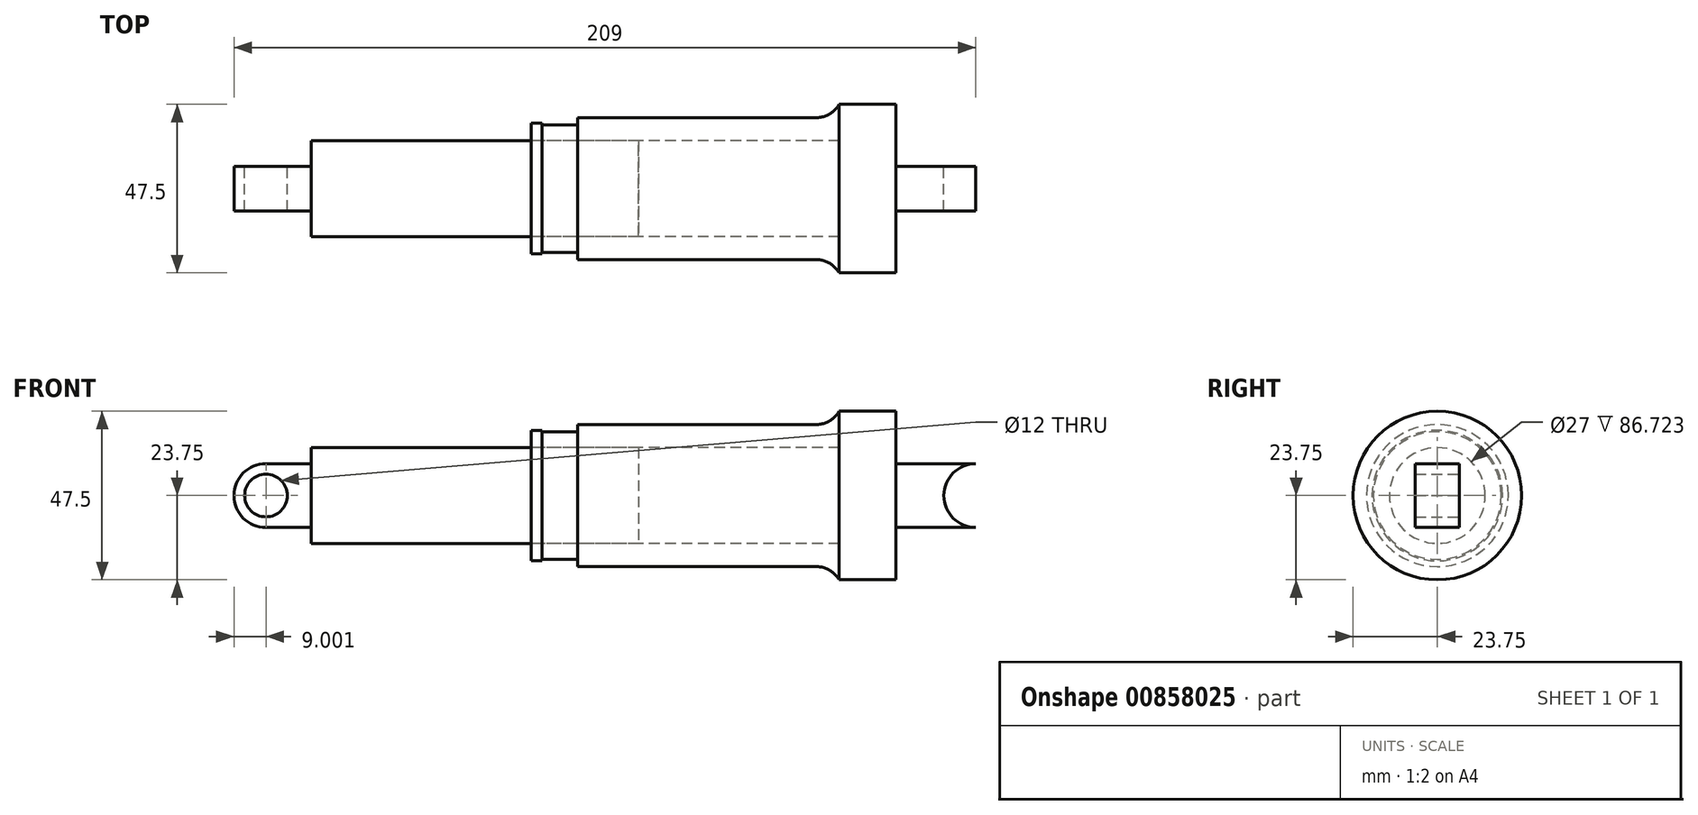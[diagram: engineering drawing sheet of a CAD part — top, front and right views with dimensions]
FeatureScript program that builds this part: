
annotation { "Feature Type Name" : "Feature", "Feature Type Description" : "" }
export const myFeature = defineFeature(function(context is Context, id is Id, definition is map)
    precondition{}
    {
        {
            var Q0;
            Q0=qCreatedBy(makeId("Front.planeOp"),FACE);
            var sketch = newSketch(context, id + "F0", { "sketchPlane" : qUnion([Q0])});
            skLineSegment(sketch, "E0.bottom", {"start": v(-74.36, -6.75) * mm, "end": v(74.36, -6.75) * mm});
            skLineSegment(sketch, "E0.top", {"start": v(-74.36, 6.75) * mm, "end": v(74.36, 6.75) * mm});
            skLineSegment(sketch, "E0.left", {"start": v(-74.36, -6.75) * mm, "end": v(-74.36, 6.75) * mm});
            skLineSegment(sketch, "E0.right", {"start": v(74.36, -6.75) * mm, "end": v(74.36, 6.75) * mm});
            skPoint(sketch, "E0.middle", {"position": v(0, 0) * mm});
            skLineSegment(sketch, "E1", {"start": v(-12.36, 6.75) * mm, "end": v(-12.36, -6.75) * mm});
            skLineSegment(sketch, "E2", {"start": v(17.86, 6.75) * mm, "end": v(17.86, -6.75) * mm});
            skLineSegment(sketch, "E3", {"start": v(-74.36, -6.75) * mm, "end": v(-87.14, -6.75) * mm});
            skLineSegment(sketch, "E4", {"start": v(-74.36, -6.75) * mm, "end": v(-74.4, -15.75) * mm});
            skLineSegment(sketch, "E5", {"start": v(-12.36, 6.75) * mm, "end": v(-12.36, 11.65) * mm});
            skLineSegment(sketch, "E6", {"start": v(-12.36, 11.65) * mm, "end": v(-9.36, 11.65) * mm});
            skLineSegment(sketch, "E7", {"start": v(-9.36, 11.65) * mm, "end": v(-9.36, 11.25) * mm});
            skLineSegment(sketch, "E8", {"start": v(-9.36, 11.25) * mm, "end": v(0.64, 11.25) * mm});
            skLineSegment(sketch, "E9", {"start": v(0.64, 11.25) * mm, "end": v(0.64, 13.25) * mm});
            skLineSegment(sketch, "E10", {"start": v(0.64, 13.25) * mm, "end": v(67.86, 13.25) * mm});
            skArc(sketch, "E11", {"start": v(67.86, 13.25) * mm, "mid": v(71.61, 14.25) * mm, "end": v(74.36, 17) * mm});
            skLineSegment(sketch, "E12", {"start": v(74.36, 17) * mm, "end": v(90.36, 17) * mm});
            skLineSegment(sketch, "E13", {"start": v(74.36, -6.75) * mm, "end": v(112.86, -6.75) * mm});
            skLineSegment(sketch, "E14", {"start": v(90.36, 17) * mm, "end": v(90.36, -6.75) * mm});
            skArc(sketch, "E15", {"start": v(112.86, 2.25) * mm, "mid": v(121.86, -6.75) * mm, "end": v(112.86, -15.75) * mm});
            skArc(sketch, "E16", {"start": v(112.86, 2.25) * mm, "mid": v(103.86, -6.75) * mm, "end": v(112.86, -15.75) * mm});
            skArc(sketch, "E17", {"start": v(-87.14, 2.25) * mm, "mid": v(-96.14, -6.75) * mm, "end": v(-87.14, -15.75) * mm});
            skPoint(sketch, "E17.startSnap0", {"position": v(-87.14, -6.75) * mm});
            skArc(sketch, "E18", {"start": v(-87.14, 2.25) * mm, "mid": v(-78.14, -6.75) * mm, "end": v(-87.14, -15.75) * mm});
            skLineSegment(sketch, "E19", {"start": v(-87.14, 2.25) * mm, "end": v(-74.36, 2.25) * mm});
            skLineSegment(sketch, "E20", {"start": v(-87.14, -15.75) * mm, "end": v(-74.4, -15.75) * mm});
            skLineSegment(sketch, "E21", {"start": v(112.86, 2.25) * mm, "end": v(90.36, 2.25) * mm});
            skLineSegment(sketch, "E22", {"start": v(112.86, -15.75) * mm, "end": v(90.36, -15.75) * mm});
            skLineSegment(sketch, "E23", {"start": v(90.36, -6.75) * mm, "end": v(90.36, -15.75) * mm});
            skArc(sketch, "E24.0", {"start": v(112.86, -0.75) * mm, "mid": v(118.86, -6.75) * mm, "end": v(112.86, -12.75) * mm});
            skArc(sketch, "E24.1", {"start": v(112.86, -0.75) * mm, "mid": v(106.86, -6.75) * mm, "end": v(112.86, -12.75) * mm});
            skArc(sketch, "E25.0", {"start": v(-87.14, -0.75) * mm, "mid": v(-93.14, -6.75) * mm, "end": v(-87.14, -12.75) * mm});
            skArc(sketch, "E25.1", {"start": v(-87.14, -0.75) * mm, "mid": v(-81.14, -6.75) * mm, "end": v(-87.14, -12.75) * mm});
            skSolve(sketch);
        }
        {
            var Q0;
            {var subQ3=sQuery(id+"F0.wireOp",EDGE,"E0.right");Q0=makeQuery(id+"F0.imprint","IMPRINT",FACE,{"disambiguationData":[TD([[makeQuery(id+"F0.imprint","IMPRINT",EDGE,{"derivedFrom":subQ3}),-1.0]])]});}
            var Q1;
            Q1=sQuery(id+"F0.wireOp",EDGE,"E13");
            revolve(context, id + "F1", {"surfaceOperationType" : NewSurfaceOperationType.NEW, "entities" : qUnion([Q0]), "axis" : qUnion([Q1]), "revolveType" : RevolveType.FULL});
        }
        {
            var Q0;
            {var subQ6=sQuery(id+"F0.wireOp",EDGE,"E1");Q0=makeQuery(id+"F0.imprint","IMPRINT",FACE,{"disambiguationData":[TD([[makeQuery(id+"F0.imprint","IMPRINT",EDGE,{"derivedFrom":subQ6}),-1.0]])]});}
            var Q1;
            {var subQ0=sQuery(id+"F0.wireOp",EDGE,"E1");Q1=makeQuery(id+"F0.imprint","IMPRINT",FACE,{"disambiguationData":[TD([[makeQuery(id+"F0.imprint","IMPRINT",EDGE,{"derivedFrom":subQ0}),1.0]])]});}
            var Q2;
            Q2=sQuery(id+"F0.wireOp",EDGE,"E0.bottom");
            revolve(context, id + "F2", {"surfaceOperationType" : NewSurfaceOperationType.NEW, "entities" : qUnion([Q0, Q1]), "axis" : qUnion([Q2]), "revolveType" : RevolveType.FULL});
        }
        {
            var Q0;
            {var subQ0=sQuery(id+"F0.wireOp",EDGE,"E17");Q0=makeQuery(id+"F0.imprint","IMPRINT",FACE,{"disambiguationData":[TD([[makeQuery(id+"F0.imprint","IMPRINT",EDGE,{"derivedFrom":subQ0}),1.0]])]});}
            var Q1;
            {var subQ3=sQuery(id+"F0.wireOp",EDGE,"E19");Q1=makeQuery(id+"F0.imprint","IMPRINT",FACE,{"disambiguationData":[TD([[makeQuery(id+"F0.imprint","IMPRINT",EDGE,{"derivedFrom":subQ3}),-1.0]])]});}
            var Q2;
            {var subQ0=sQuery(id+"F0.wireOp",EDGE,"E4");Q2=makeQuery(id+"F0.imprint","IMPRINT",FACE,{"disambiguationData":[TD([[makeQuery(id+"F0.imprint","IMPRINT",EDGE,{"derivedFrom":subQ0}),-1.0]])]});}
            extrude(context, id + "F3", {"entities" : qUnion([Q0, Q1, Q2]), "operationType" : NewBodyOperationType.ADD, "endBound" : BoundingType.SYMMETRIC, "depth" : 12.5 * mm, "offsetDistance" : 25 * mm});
        }
        {
            var Q0;
            {var subQ5=sQuery(id+"F0.wireOp",EDGE,"E21");Q0=makeQuery(id+"F0.imprint","IMPRINT",FACE,{"disambiguationData":[TD([[makeQuery(id+"F0.imprint","IMPRINT",EDGE,{"derivedFrom":subQ5}),1.0]])]});}
            var Q1;
            {var subQ4=sQuery(id+"F0.wireOp",EDGE,"E22");Q1=makeQuery(id+"F0.imprint","IMPRINT",FACE,{"disambiguationData":[TD([[makeQuery(id+"F0.imprint","IMPRINT",EDGE,{"derivedFrom":subQ4}),-1.0]])]});}
            var Q2;
            {var subQ0=sQuery(id+"F0.wireOp",EDGE,"E15");Q2=makeQuery(id+"F0.imprint","IMPRINT",FACE,{"disambiguationData":[TD([[makeQuery(id+"F0.imprint","IMPRINT",EDGE,{"derivedFrom":subQ0}),-1.0]])]});}
            extrude(context, id + "F4", {"entities" : qUnion([Q0, Q1, Q2]), "operationType" : NewBodyOperationType.ADD, "endBound" : BoundingType.SYMMETRIC, "depth" : 12.5 * mm, "offsetDistance" : 25 * mm});
        }
    });
